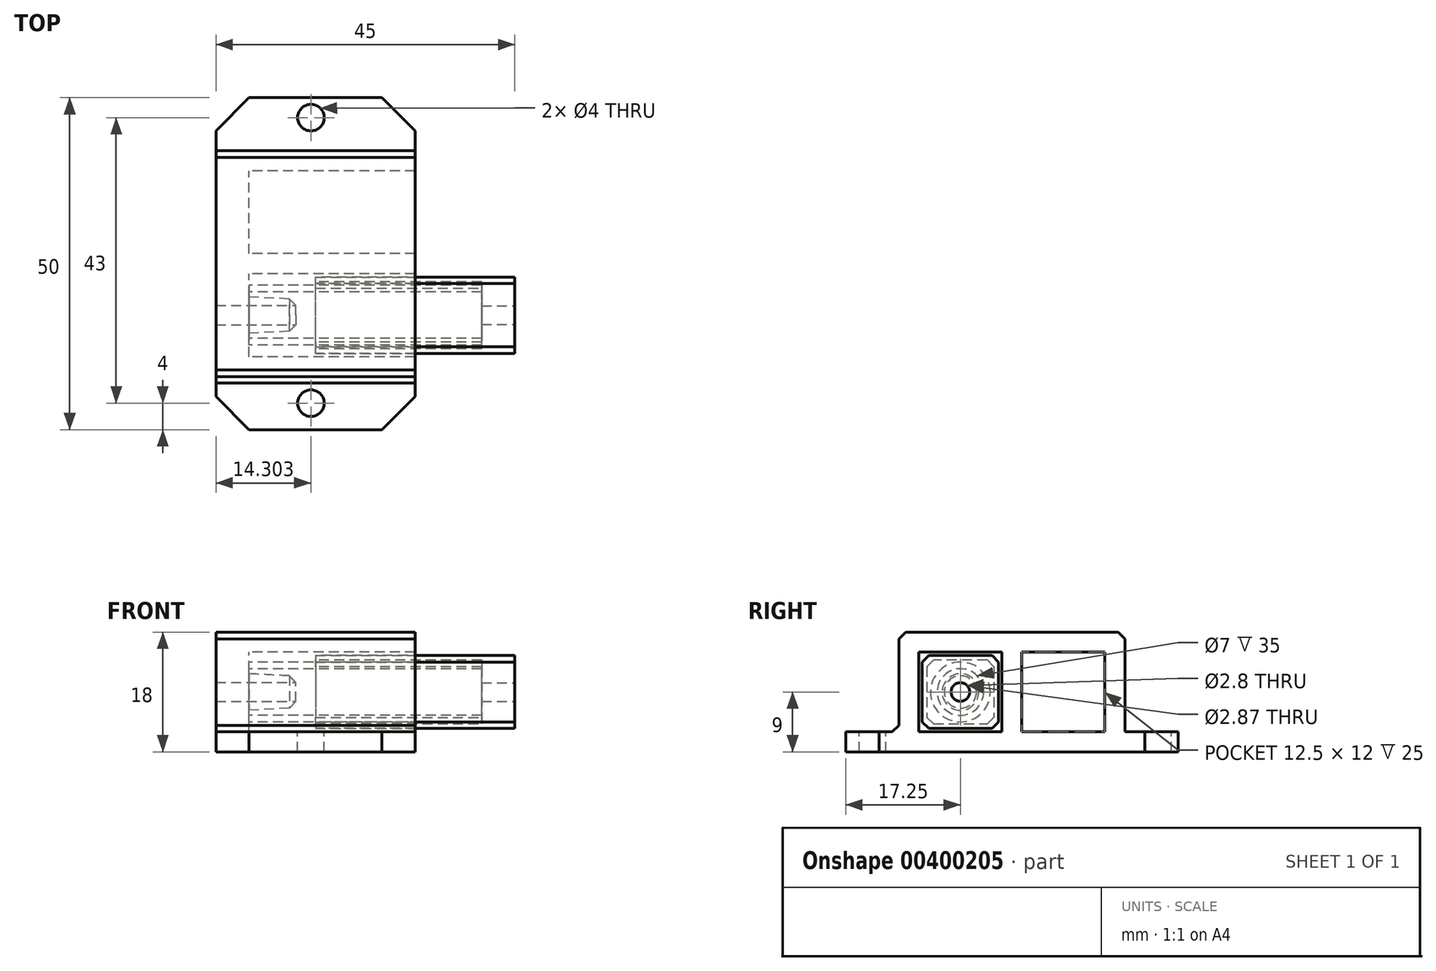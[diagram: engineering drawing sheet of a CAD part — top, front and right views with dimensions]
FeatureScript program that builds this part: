
annotation { "Feature Type Name" : "Feature", "Feature Type Description" : "" }
export const myFeature = defineFeature(function(context is Context, id is Id, definition is map)
    precondition{}
    {
        {
            var Q0;
            Q0=qCreatedBy(makeId("Top.planeOp"),FACE);
            var sketch = newSketch(context, id + "F0", { "sketchPlane" : qUnion([Q0])});
            skLineSegment(sketch, "E0.bottom", {"start": v(0, 0) * mm, "end": v(30, 0) * mm});
            skLineSegment(sketch, "E0.top", {"start": v(0, 50) * mm, "end": v(30, 50) * mm});
            skLineSegment(sketch, "E0.left", {"start": v(0, 0) * mm, "end": v(0, 50) * mm});
            skLineSegment(sketch, "E0.right", {"start": v(30, 0) * mm, "end": v(30, 50) * mm});
            skSolve(sketch);
        }
        {
            var Q0;
            Q0=makeQuery(id+"F0.imprint","IMPRINT",FACE,{"disambiguationData":[TD([[makeQuery(id+"F0.imprint","IMPRINT",EDGE,{"derivedFrom":sQuery(id+"F0.wireOp",EDGE,"E0.bottom")}),1.0]])]});
            extrude(context, id + "F1", {"entities" : qUnion([Q0]), "depth" : 3 * mm});
        }
        {
            var Q0;
            Q0=makeQuery(id+"F1.opExtrude","CAP_FACE",FACE,{"disambiguationData":[OSD([sQuery(id+"F0.wireOp",EDGE,"E0.bottom"),sQuery(id+"F0.wireOp",EDGE,"E0.top"),sQuery(id+"F0.wireOp",EDGE,"E0.left"),sQuery(id+"F0.wireOp",EDGE,"E0.right")])],"isStart":false});
            var sketch = newSketch(context, id + "F2", { "sketchPlane" : qUnion([Q0])});
            skCircle(sketch, "E1", {"center": v(14.3, 47) * mm, "radius": 2 * mm});
            skCircle(sketch, "E2", {"center": v(14.3, 4) * mm, "radius": 2 * mm});
            skLineSegment(sketch, "E3", {"start": v(14.3, 4) * mm, "end": v(14.3, 0) * mm, "construction": true});
            skSolve(sketch);
        }
        {
            var Q0;
            Q0 = qSketchRegion(id + "F2", true);
            extrude(context, id + "F3", {"entities" : qUnion([Q0]), "operationType" : NewBodyOperationType.REMOVE, "endBound" : BoundingType.THROUGH_ALL, "oppositeDirection" : true, "depth" : 25 * mm});
        }
        {
            var Q0;
            Q0=makeQuery(id+"F1.opExtrude","SWEPT_FACE",FACE,{"disambiguationData":[OSD([sQuery(id+"F0.wireOp",EDGE,"E0.left")])]});
            var sketch = newSketch(context, id + "F4", { "sketchPlane" : qUnion([Q0])});
            skLineSegment(sketch, "E4.top", {"start": v(-8, 18) * mm, "end": v(-42, 18) * mm});
            skLineSegment(sketch, "E4.left", {"start": v(-8, 3) * mm, "end": v(-8, 18) * mm});
            skLineSegment(sketch, "E4.right", {"start": v(-42, 3) * mm, "end": v(-42, 18) * mm});
            skLineSegment(sketch, "E5.top", {"start": v(-11, 15) * mm, "end": v(-23.5, 15) * mm});
            skLineSegment(sketch, "E5.left", {"start": v(-11, 3) * mm, "end": v(-11, 15) * mm});
            skLineSegment(sketch, "E5.right", {"start": v(-23.5, 3) * mm, "end": v(-23.5, 15) * mm});
            skLineSegment(sketch, "E6.top", {"start": v(-26.5, 15) * mm, "end": v(-39, 15) * mm});
            skLineSegment(sketch, "E6.left", {"start": v(-26.5, 3) * mm, "end": v(-26.5, 15) * mm});
            skLineSegment(sketch, "E6.right", {"start": v(-39, 3) * mm, "end": v(-39, 15) * mm});
            skLineSegment(sketch, "E7", {"start": v(-11, 3) * mm, "end": v(-8, 3) * mm});
            skLineSegment(sketch, "E8", {"start": v(-23.5, 3) * mm, "end": v(-26.5, 3) * mm});
            skLineSegment(sketch, "E9", {"start": v(-39, 3) * mm, "end": v(-42, 3) * mm});
            skSolve(sketch);
        }
        {
            var Q0;
            Q0=makeQuery(id+"F4.imprint","IMPRINT",FACE,{"disambiguationData":[TD([[makeQuery(id+"F4.imprint","IMPRINT",EDGE,{"derivedFrom":sQuery(id+"F4.wireOp",EDGE,"E4.top")}),1.0]])]});
            var Q1;
            Q1=makeQuery(id+"F1.opExtrude","SWEPT_FACE",FACE,{"disambiguationData":[OSD([sQuery(id+"F0.wireOp",EDGE,"E0.right")])]});
            extrude(context, id + "F5", {"entities" : qUnion([Q0]), "operationType" : NewBodyOperationType.ADD, "endBound" : BoundingType.UP_TO_SURFACE, "oppositeDirection" : true, "endBoundEntityFace" : qUnion([Q1]), "depth" : 25 * mm});
        }
        {
            var Q0;
            Q0=makeQuery(id+"F5.boolean.opBoolean","MERGE",FACE,{"derivedFrom":[makeQuery(id+"F1.opExtrude","SWEPT_FACE",FACE,{"disambiguationData":[OSD([sQuery(id+"F0.wireOp",EDGE,"E0.left")])]}),makeQuery(id+"F5.opExtrude","CAP_FACE",FACE,{"disambiguationData":[OSD([sQuery(id+"F4.wireOp",EDGE,"E4.top"),sQuery(id+"F4.wireOp",EDGE,"E4.left"),sQuery(id+"F4.wireOp",EDGE,"E4.right"),sQuery(id+"F4.wireOp",EDGE,"E5.top"),sQuery(id+"F4.wireOp",EDGE,"E5.left"),sQuery(id+"F4.wireOp",EDGE,"E5.right"),sQuery(id+"F4.wireOp",EDGE,"E6.top"),sQuery(id+"F4.wireOp",EDGE,"E6.left"),sQuery(id+"F4.wireOp",EDGE,"E6.right"),sQuery(id+"F4.wireOp",EDGE,"E7"),sQuery(id+"F4.wireOp",EDGE,"E8"),sQuery(id+"F4.wireOp",EDGE,"E9")])],"isStart":true})]});
            var sketch = newSketch(context, id + "F6", { "sketchPlane" : qUnion([Q0])});
            skLineSegment(sketch, "E10.0", {"start": v(-11, 15) * mm, "end": v(-23.5, 15) * mm});
            skLineSegment(sketch, "E11.0.1", {"start": v(-11, 15) * mm, "end": v(-11, 3) * mm});
            skLineSegment(sketch, "E11.0.3", {"start": v(-11, 3) * mm, "end": v(-11, 15) * mm});
            skLineSegment(sketch, "E12.0.0", {"start": v(-50, 0) * mm, "end": v(0, 0) * mm, "construction": true});
            skLineSegment(sketch, "E12.0.1", {"start": v(0, 0) * mm, "end": v(0, 3) * mm, "construction": true});
            skLineSegment(sketch, "E12.0.2", {"start": v(0, 3) * mm, "end": v(-8, 3) * mm, "construction": true});
            skLineSegment(sketch, "E12.0.3", {"start": v(-8, 3) * mm, "end": v(-8, 18) * mm, "construction": true});
            skLineSegment(sketch, "E12.0.4", {"start": v(-8, 18) * mm, "end": v(-42, 18) * mm, "construction": true});
            skLineSegment(sketch, "E12.0.5", {"start": v(-42, 18) * mm, "end": v(-42, 3) * mm, "construction": true});
            skLineSegment(sketch, "E12.0.6", {"start": v(-42, 3) * mm, "end": v(-50, 3) * mm, "construction": true});
            skLineSegment(sketch, "E12.0.7", {"start": v(-50, 3) * mm, "end": v(-50, 0) * mm, "construction": true});
            skLineSegment(sketch, "E13.0", {"start": v(-23.5, 3) * mm, "end": v(-23.5, 15) * mm});
            skPoint(sketch, "E14.0", {"position": v(-17.25, 3) * mm});
            skLineSegment(sketch, "E15.0", {"start": v(-26.5, 3) * mm, "end": v(-39, 3) * mm});
            skLineSegment(sketch, "E16.0", {"start": v(-26.5, 3) * mm, "end": v(-26.5, 15) * mm});
            skLineSegment(sketch, "E17.0", {"start": v(-26.5, 15) * mm, "end": v(-39, 15) * mm});
            skLineSegment(sketch, "E18.0", {"start": v(-39, 3) * mm, "end": v(-39, 15) * mm});
            skLineSegment(sketch, "E19.0", {"start": v(-11, 3) * mm, "end": v(-23.5, 3) * mm});
            skSolve(sketch);
        }
        {
            var Q0;
            Q0 = qSketchRegion(id + "F6", true);
            extrude(context, id + "F7", {"entities" : qUnion([Q0]), "operationType" : NewBodyOperationType.ADD, "oppositeDirection" : true, "depth" : 5 * mm});
        }
        {
            var Q0;
            Q0=makeQuery(id+"F7.opExtrude","CAP_FACE",FACE,{"disambiguationData":[OSD([sQuery(id+"F6.wireOp",EDGE,"E10.0"),sQuery(id+"F6.wireOp",EDGE,"E11.0.3"),sQuery(id+"F6.wireOp",EDGE,"E13.0"),sQuery(id+"F6.wireOp",EDGE,"E19.0")])],"isStart":false});
            var sketch = newSketch(context, id + "F8", { "sketchPlane" : qUnion([Q0])});
            skCircle(sketch, "E20", {"center": v(17.25, 9) * mm, "radius": 2.75 * mm});
            skLineSegment(sketch, "E21", {"start": v(17.25, 9) * mm, "end": v(17.25, 3) * mm, "construction": true});
            skLineSegment(sketch, "E22", {"start": v(17.25, 9) * mm, "end": v(23.5, 9) * mm, "construction": true});
            skSolve(sketch);
        }
        {
            var Q0;
            Q0=makeQuery(id+"F8.imprint","IMPRINT",FACE,{"disambiguationData":[TD([[makeQuery(id+"F8.imprint","IMPRINT",EDGE,{"derivedFrom":sQuery(id+"F8.wireOp",EDGE,"E20")}),1.0]])]});
            extrude(context, id + "F9", {"entities" : qUnion([Q0]), "operationType" : NewBodyOperationType.ADD, "depth" : 7 * mm, "hasDraft" : true, "draftAngle" : 3 * degree, "draftPullDirection" : true});
        }
        {
            var Q0;
            Q0=makeQuery(id+"F9.opExtrude","CAP_EDGE",EDGE,{"disambiguationData":[OSD([sQuery(id+"F8.wireOp",EDGE,"E20")])],"isStart":false});
            chamfer(context, id + "F10", {"entities" : qUnion([Q0]), "width" : 1 * mm, "tangentPropagation" : true});
        }
        {
            var Q0;
            Q0=makeQuery(id+"F9.opExtrude","CAP_FACE",FACE,{"disambiguationData":[OSD([sQuery(id+"F8.wireOp",EDGE,"E20")])],"isStart":false});
            extrude(context, id + "F11", {"entities" : qUnion([Q0]), "operationType" : NewBodyOperationType.REMOVE, "endBound" : BoundingType.THROUGH_ALL, "oppositeDirection" : true, "depth" : 25 * mm});
        }
        {
            var Q0;
            Q0=makeQuery(id+"F5.opExtrude","CAP_EDGE",EDGE,{"disambiguationData":[OSD([sQuery(id+"F4.wireOp",EDGE,"E4.top")])],"isStart":false});
            cPoint(context, id + "F12", {"entities" : qUnion([Q0]), "parameter" : 0.5});
        }
        {
            var Q0;
            Q0=makeQuery(id+"F1.opExtrude","CAP_EDGE",EDGE,{"disambiguationData":[OSD([sQuery(id+"F0.wireOp",EDGE,"E0.right")])],"isStart":true});
            cPoint(context, id + "F13", {"entities" : qUnion([Q0]), "parameter" : 0.5});
        }
        {
            var Q0;
            Q0=makeQuery(id+"F5.opExtrude","CAP_EDGE",EDGE,{"disambiguationData":[OSD([sQuery(id+"F4.wireOp",EDGE,"E4.top")])],"isStart":true});
            cPoint(context, id + "F14", {"entities" : qUnion([Q0]), "parameter" : 0.5});
        }
        {
            var Q0;
            Q0 = qCreatedBy(id + "F12" ,VERTEX);
            var Q1;
            Q1 = qCreatedBy(id + "F13" ,VERTEX);
            var Q2;
            Q2 = qCreatedBy(id + "F14" ,VERTEX);
            cPlane(context, id + "F15", {"entities" : qUnion([Q0, Q1, Q2]), "cplaneType" : CPlaneType.THREE_POINT, "offset" : 25 * mm, "width" : 150 * mm, "height" : 150 * mm});
        }
        {
            var Q0;
            Q0=makeQuery(id+"F7.opExtrude","CAP_FACE",FACE,{"disambiguationData":[OSD([sQuery(id+"F6.wireOp",EDGE,"E10.0"),sQuery(id+"F6.wireOp",EDGE,"E11.0.3"),sQuery(id+"F6.wireOp",EDGE,"E13.0"),sQuery(id+"F6.wireOp",EDGE,"E19.0")])],"isStart":false});
            var sketch = newSketch(context, id + "F16", { "sketchPlane" : qUnion([Q0])});
            skCircle(sketch, "E23.0", {"center": v(17.25, 9) * mm, "radius": 2.75 * mm});
            skCircle(sketch, "E24", {"center": v(17.25, 9) * mm, "radius": 3.5 * mm});
            skCircle(sketch, "E25", {"center": v(17.25, 9) * mm, "radius": 4.5 * mm});
            skSolve(sketch);
        }
        {
            var Q0;
            Q0=makeQuery(id+"F16.imprint","IMPRINT",FACE,{"disambiguationData":[TD([[makeQuery(id+"F16.imprint","IMPRINT",EDGE,{"derivedFrom":sQuery(id+"F16.wireOp",EDGE,"E24")}),-1.0]])]});
            extrude(context, id + "F17", {"entities" : qUnion([Q0]), "depth" : 35 * mm});
        }
        {
            var Q0;
            Q0=makeQuery(id+"F17.opExtrude","CAP_FACE",FACE,{"disambiguationData":[OSD([sQuery(id+"F16.wireOp",EDGE,"E24"),sQuery(id+"F16.wireOp",EDGE,"E25")])],"isStart":false});
            var sketch = newSketch(context, id + "F18", { "sketchPlane" : qUnion([Q0])});
            skLineSegment(sketch, "E26.0", {"start": v(11, 3) * mm, "end": v(23.5, 3) * mm, "construction": true});
            skLineSegment(sketch, "E27.0", {"start": v(23.5, 15) * mm, "end": v(23.5, 3) * mm, "construction": true});
            skLineSegment(sketch, "E28.0", {"start": v(11, 15) * mm, "end": v(11, 3) * mm, "construction": true});
            skLineSegment(sketch, "E29.0", {"start": v(23.5, 15) * mm, "end": v(11, 15) * mm, "construction": true});
            skLineSegment(sketch, "E30.0", {"start": v(11.5, 3.5) * mm, "end": v(23, 3.5) * mm});
            skLineSegment(sketch, "E30.1", {"start": v(11.5, 14.5) * mm, "end": v(11.5, 3.5) * mm});
            skLineSegment(sketch, "E30.2", {"start": v(23, 14.5) * mm, "end": v(11.5, 14.5) * mm});
            skLineSegment(sketch, "E30.3", {"start": v(23, 14.5) * mm, "end": v(23, 3.5) * mm});
            skLineSegment(sketch, "E31.0", {"start": v(12.2, 4.2) * mm, "end": v(22.3, 4.2) * mm});
            skLineSegment(sketch, "E31.1", {"start": v(12.2, 13.8) * mm, "end": v(12.2, 4.2) * mm});
            skLineSegment(sketch, "E31.2", {"start": v(22.3, 13.8) * mm, "end": v(12.2, 13.8) * mm});
            skLineSegment(sketch, "E31.3", {"start": v(22.3, 13.8) * mm, "end": v(22.3, 4.2) * mm});
            skSolve(sketch);
        }
        {
            var Q0;
            Q0 = qSketchRegion(id + "F18", true);
            extrude(context, id + "F19", {"entities" : qUnion([Q0]), "oppositeDirection" : true, "depth" : 25 * mm});
        }
        {
            var Q0;
            Q0=makeQuery(id+"F19.opExtrude","CAP_FACE",FACE,{"disambiguationData":[OSD([sQuery(id+"F18.wireOp",EDGE,"E30.0"),sQuery(id+"F18.wireOp",EDGE,"E30.1"),sQuery(id+"F18.wireOp",EDGE,"E30.2"),sQuery(id+"F18.wireOp",EDGE,"E30.3"),sQuery(id+"F18.wireOp",EDGE,"E31.0"),sQuery(id+"F18.wireOp",EDGE,"E31.1"),sQuery(id+"F18.wireOp",EDGE,"E31.2"),sQuery(id+"F18.wireOp",EDGE,"E31.3")])],"isStart":true});
            var sketch = newSketch(context, id + "F20", { "sketchPlane" : qUnion([Q0])});
            skLineSegment(sketch, "E32.0", {"start": v(11.5, 3.5) * mm, "end": v(23, 3.5) * mm});
            skLineSegment(sketch, "E33.0", {"start": v(11.5, 14.5) * mm, "end": v(11.5, 3.5) * mm});
            skLineSegment(sketch, "E34.0", {"start": v(23, 14.5) * mm, "end": v(11.5, 14.5) * mm});
            skLineSegment(sketch, "E35.0", {"start": v(23, 14.5) * mm, "end": v(23, 3.5) * mm});
            skSolve(sketch);
        }
        {
            var Q0;
            Q0 = qSketchRegion(id + "F20", true);
            extrude(context, id + "F21", {"entities" : qUnion([Q0]), "operationType" : NewBodyOperationType.ADD, "depth" : 5 * mm});
        }
        {
            var Q0;
            Q0=makeQuery(id+"F21.opExtrude","CAP_FACE",FACE,{"disambiguationData":[OSD([sQuery(id+"F20.wireOp",EDGE,"E32.0"),sQuery(id+"F20.wireOp",EDGE,"E33.0"),sQuery(id+"F20.wireOp",EDGE,"E34.0"),sQuery(id+"F20.wireOp",EDGE,"E35.0")])],"isStart":false});
            var sketch = newSketch(context, id + "F22", { "sketchPlane" : qUnion([Q0])});
            skLineSegment(sketch, "E36", {"start": v(11.5, 3.5) * mm, "end": v(23, 14.5) * mm, "construction": true});
            skCircle(sketch, "E37", {"center": v(17.25, 9) * mm, "radius": 1.4 * mm});
            skSolve(sketch);
        }
        {
            var Q0;
            Q0 = qSketchRegion(id + "F22", true);
            extrude(context, id + "F23", {"entities" : qUnion([Q0]), "operationType" : NewBodyOperationType.REMOVE, "endBound" : BoundingType.THROUGH_ALL, "oppositeDirection" : true, "depth" : 25 * mm});
        }
        {
            var Q0;
            Q0=makeQuery(id+"F21.boolean.opBoolean","MERGE",EDGE,{"derivedFrom":[makeQuery(id+"F19.opExtrude","SWEPT_EDGE",EDGE,{"disambiguationData":[OSD([sQuery(id+"F18.wireOp",EDGE,"E30.2"),sQuery(id+"F18.wireOp",EDGE,"E30.3")])]}),makeQuery(id+"F21.opExtrude","SWEPT_EDGE",EDGE,{"disambiguationData":[OSD([sQuery(id+"F20.wireOp",EDGE,"E34.0"),sQuery(id+"F20.wireOp",EDGE,"E35.0")])]})]});
            var Q1;
            Q1=makeQuery(id+"F21.boolean.opBoolean","MERGE",EDGE,{"derivedFrom":[makeQuery(id+"F19.opExtrude","SWEPT_EDGE",EDGE,{"disambiguationData":[OSD([sQuery(id+"F18.wireOp",EDGE,"E30.1"),sQuery(id+"F18.wireOp",EDGE,"E30.2")])]}),makeQuery(id+"F21.opExtrude","SWEPT_EDGE",EDGE,{"disambiguationData":[OSD([sQuery(id+"F20.wireOp",EDGE,"E33.0"),sQuery(id+"F20.wireOp",EDGE,"E34.0")])]})]});
            var Q2;
            Q2=makeQuery(id+"F21.boolean.opBoolean","MERGE",EDGE,{"derivedFrom":[makeQuery(id+"F19.opExtrude","SWEPT_EDGE",EDGE,{"disambiguationData":[OSD([sQuery(id+"F18.wireOp",EDGE,"E30.0"),sQuery(id+"F18.wireOp",EDGE,"E30.1")])]}),makeQuery(id+"F21.opExtrude","SWEPT_EDGE",EDGE,{"disambiguationData":[OSD([sQuery(id+"F20.wireOp",EDGE,"E32.0"),sQuery(id+"F20.wireOp",EDGE,"E33.0")])]})]});
            var Q3;
            Q3=makeQuery(id+"F21.boolean.opBoolean","MERGE",EDGE,{"derivedFrom":[makeQuery(id+"F19.opExtrude","SWEPT_EDGE",EDGE,{"disambiguationData":[OSD([sQuery(id+"F18.wireOp",EDGE,"E30.0"),sQuery(id+"F18.wireOp",EDGE,"E30.3")])]}),makeQuery(id+"F21.opExtrude","SWEPT_EDGE",EDGE,{"disambiguationData":[OSD([sQuery(id+"F20.wireOp",EDGE,"E32.0"),sQuery(id+"F20.wireOp",EDGE,"E35.0")])]})]});
            chamfer(context, id + "F24", {"entities" : qUnion([Q0, Q1, Q2, Q3]), "width" : 1 * mm, "tangentPropagation" : true});
        }
        {
            var Q0;
            Q0=makeQuery(id+"F1.opExtrude","SWEPT_EDGE",EDGE,{"disambiguationData":[OSD([sQuery(id+"F0.wireOp",EDGE,"E0.bottom"),sQuery(id+"F0.wireOp",EDGE,"E0.left")])]});
            var Q1;
            Q1=makeQuery(id+"F1.opExtrude","SWEPT_EDGE",EDGE,{"disambiguationData":[OSD([sQuery(id+"F0.wireOp",EDGE,"E0.bottom"),sQuery(id+"F0.wireOp",EDGE,"E0.right")])]});
            var Q2;
            Q2=makeQuery(id+"F1.opExtrude","SWEPT_EDGE",EDGE,{"disambiguationData":[OSD([sQuery(id+"F0.wireOp",EDGE,"E0.top"),sQuery(id+"F0.wireOp",EDGE,"E0.right")])]});
            var Q3;
            Q3=makeQuery(id+"F1.opExtrude","SWEPT_EDGE",EDGE,{"disambiguationData":[OSD([sQuery(id+"F0.wireOp",EDGE,"E0.top"),sQuery(id+"F0.wireOp",EDGE,"E0.left")])]});
            chamfer(context, id + "F25", {"entities" : qUnion([Q0, Q1, Q2, Q3]), "width" : 5 * mm, "tangentPropagation" : true});
        }
        {
            var Q0;
            Q0=makeQuery(id+"F5.opExtrude","SWEPT_EDGE",EDGE,{"disambiguationData":[OSD([sQuery(id+"F4.wireOp",EDGE,"E4.top"),sQuery(id+"F4.wireOp",EDGE,"E4.right")])]});
            var Q1;
            Q1=makeQuery(id+"F5.opExtrude","SWEPT_EDGE",EDGE,{"disambiguationData":[OSD([sQuery(id+"F0.wireOp",EDGE,"E0.left"),sQuery(id+"F4.wireOp",EDGE,"E4.right"),sQuery(id+"F4.wireOp",EDGE,"E9")])]});
            var Q2;
            Q2=makeQuery(id+"F5.opExtrude","SWEPT_EDGE",EDGE,{"disambiguationData":[OSD([sQuery(id+"F4.wireOp",EDGE,"E4.top"),sQuery(id+"F4.wireOp",EDGE,"E4.left")])]});
            var Q3;
            Q3=makeQuery(id+"F5.opExtrude","SWEPT_EDGE",EDGE,{"disambiguationData":[OSD([sQuery(id+"F0.wireOp",EDGE,"E0.left"),sQuery(id+"F4.wireOp",EDGE,"E4.left"),sQuery(id+"F4.wireOp",EDGE,"E7")])]});
            chamfer(context, id + "F26", {"entities" : qUnion([Q0, Q1, Q2, Q3]), "width" : 1 * mm, "tangentPropagation" : true});
        }
        {
            var Q0;
            Q0=makeQuery(id+"F19.opExtrude","SWEPT_EDGE",EDGE,{"disambiguationData":[OSD([sQuery(id+"F18.wireOp",EDGE,"E31.0"),sQuery(id+"F18.wireOp",EDGE,"E31.1")])]});
            var Q1;
            Q1=makeQuery(id+"F19.opExtrude","SWEPT_EDGE",EDGE,{"disambiguationData":[OSD([sQuery(id+"F18.wireOp",EDGE,"E31.0"),sQuery(id+"F18.wireOp",EDGE,"E31.3")])]});
            var Q2;
            Q2=makeQuery(id+"F19.opExtrude","SWEPT_EDGE",EDGE,{"disambiguationData":[OSD([sQuery(id+"F18.wireOp",EDGE,"E31.1"),sQuery(id+"F18.wireOp",EDGE,"E31.2")])]});
            var Q3;
            Q3=makeQuery(id+"F19.opExtrude","SWEPT_EDGE",EDGE,{"disambiguationData":[OSD([sQuery(id+"F18.wireOp",EDGE,"E31.2"),sQuery(id+"F18.wireOp",EDGE,"E31.3")])]});
            chamfer(context, id + "F27", {"entities" : qUnion([Q0, Q1, Q2, Q3]), "width" : 1 * mm, "tangentPropagation" : true});
        }
    });
